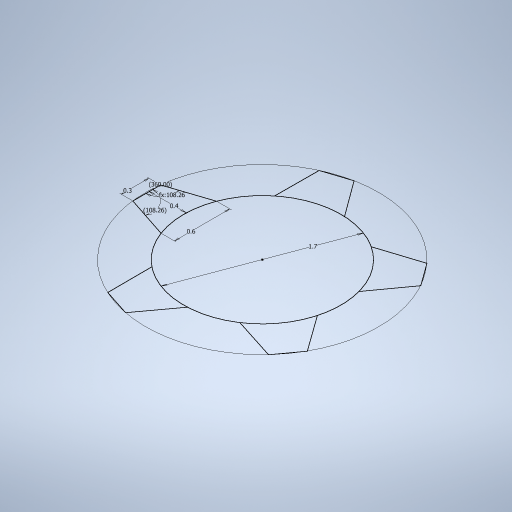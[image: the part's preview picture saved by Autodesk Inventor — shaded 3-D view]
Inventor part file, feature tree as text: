
AUTODESK INVENTOR PART (.ipt)
format: ipt  version: 2023 (Build 270158000, 158)  size: 244,224 bytes
history: native  units: in
note: dims shown in document units (in); Inventor stores cm internally (conversion verified against a paired STEP export)
features: sketch x1
ambient origin geometry x8: Origin, YZ Plane, XZ Plane, XY Plane, X Axis, Y Axis, Z Axis, Center Point
feature tree (1):
  sketch  "Sketch1"  dims[d0=0.6693in d1=0.1181in d2=0.1575in d3=0.2362in d4=0.7439in d5=0.7439in d6=1.9685in d8=360.0deg]
